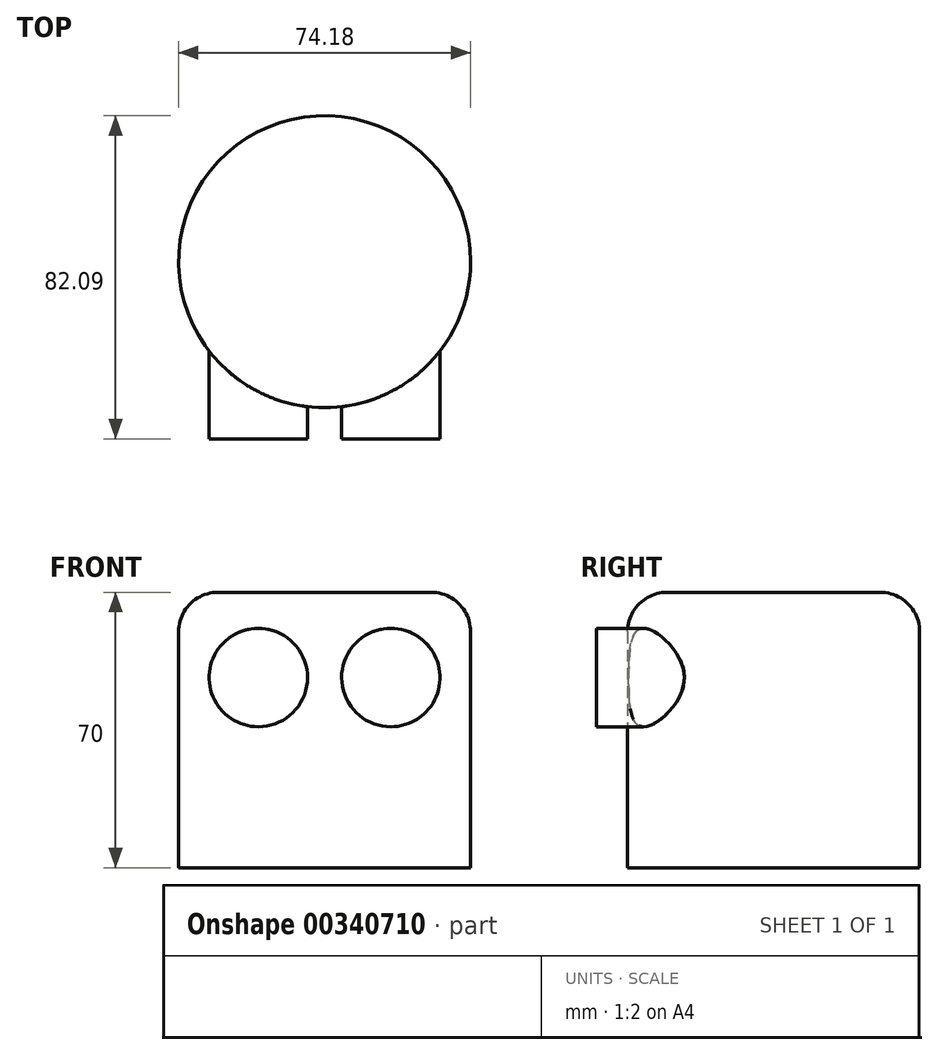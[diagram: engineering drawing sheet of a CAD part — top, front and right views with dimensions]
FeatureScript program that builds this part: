
annotation { "Feature Type Name" : "Feature", "Feature Type Description" : "" }
export const myFeature = defineFeature(function(context is Context, id is Id, definition is map)
    precondition{}
    {
        {
            var Q0;
            Q0=qCreatedBy(makeId("Top.planeOp"),FACE);
            var sketch = newSketch(context, id + "F0", { "sketchPlane" : qUnion([Q0])});
            skCircle(sketch, "E0", {"center": v(0, 0) * mm, "radius": 37.1 * mm});
            skSolve(sketch);
        }
        {
            var Q0;
            Q0=makeQuery(id+"F0.imprint","IMPRINT",FACE,{"disambiguationData":[TD([[makeQuery(id+"F0.imprint","IMPRINT",EDGE,{"derivedFrom":sQuery(id+"F0.wireOp",EDGE,"E0")}),1.0]])]});
            extrude(context, id + "F1", {"entities" : qUnion([Q0]), "depth" : 70 * mm});
        }
        {
            var Q0;
            Q0=makeQuery(id+"F1.opExtrude","CAP_FACE",FACE,{"disambiguationData":[OSD([sQuery(id+"F0.wireOp",EDGE,"E0")])],"isStart":false});
            fillet(context, id + "F2", {"entities" : qUnion([Q0]), "radius" : 10 * mm, "tangentPropagation" : true, "allowEdgeOverflow" : false});
        }
        {
            var Q0;
            Q0=qCreatedBy(makeId("Front.planeOp"),FACE);
            var sketch = newSketch(context, id + "F3", { "sketchPlane" : qUnion([Q0])});
            skCircle(sketch, "E1", {"center": v(-16.83, 48.34) * mm, "radius": 12.5 * mm});
            skCircle(sketch, "E2", {"center": v(16.83, 48.34) * mm, "radius": 12.5 * mm});
            skPoint(sketch, "E3.orphan", {"position": v(-16.83, 69.34) * mm});
            skPoint(sketch, "E4.start.orphan", {"position": v(-36.83, 48.34) * mm});
            skPoint(sketch, "E5.MirrorCS.start.orphan", {"position": v(36.83, 48.34) * mm});
            skPoint(sketch, "E6.MirrorCS.start.orphan", {"position": v(16.83, 69.34) * mm});
            skSolve(sketch);
        }
        {
            var Q0;
            Q0 = qSketchRegion(id + "F3", true);
            extrude(context, id + "F4", {"entities" : qUnion([Q0]), "operationType" : NewBodyOperationType.ADD, "depth" : 45 * mm});
        }
    });
